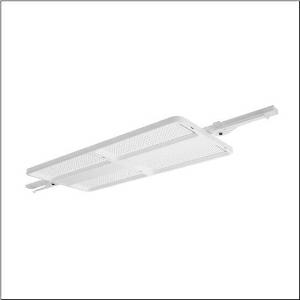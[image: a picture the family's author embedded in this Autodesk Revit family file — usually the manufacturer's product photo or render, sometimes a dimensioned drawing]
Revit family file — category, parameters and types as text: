
# Revit family: highbay_11_fur_modario_r__tragschiene_maxi_51hn11db3tma_954c
name_source: partatom
category: Lighting Fixtures
units: mm (PartAtom-declared; Revit-internal decimal feet)

## family parameters
Cut with Voids When Loaded = No
Host = Face
Light Source = No
Part Type = Normal
Room Calculation Point = No
Round Connector Dimension = Use Diameter
Shared = No

## types (1)
- --- (1 x LED, 53070 lm, 295.1 W, 3000K)
    Apparent Load = 295 VA
    CIE Flux Codes = 85 97 100 100 100
    Color Rendering = 80
    Color Temperature = 3000K
    Default Elevation = 1800 mm
    Description = high bay luminaire Highbay 11 for Modario® trunking rail maxi; direct symmetric narrow distribution, light control with lens of PMMA; UGR ≤ 22 (X = 4H | Y = 8H | S = 0.25H | reflection values 70/50/20); luminous flux: 53.070lm; light colour: 830, colour temperature: 3000K, MacAdam ≤ 2 SDCM (initial), colour rendering: CRI > 80; luminous efficacy: 179,8lm/W; rated service life: 100.000h (L95/B50) at AT= 25°C; control: DALI 2; luminaire connection: plug, 5-pole, with phase selectionmains connection: 230..240V, AC 50/60Hz; connected load: 295,1W; protection rating (complete): IP64; insulation class (complete): insulation class I (protective earthing); protection symbol: D; impact resistance: IK07; certification: CE, ENEC, VDE, UKCA; internal wiring halogen-free; luminaire corresponds to IFS (International Featured Standards) requirements for safety and quality in the food industry; LABS conformity tested according to VDMA 24364:2018-05; housing frame of high-performance plastic PA6, matt traffic white (RAL 9016); cover of PMMA; fixing on rail side of steel, galvanised, white; blank cover of PC, traffic white (RAL 9016); dimension (LxWxH): 1.496 x 442 x 72mm; permissible operating ambient temperature: -40..+50°C (reducing of maximum allowable ambient temperature of 5°C with ceiling mounting); packaging unit: 1 piece
    Height = 72 mm  [stored 0.23622 ft]
    Lamp = 1 x LED
    Lamp Light Flux = 53070 lm
    Lamp Power = 295.1 W
    Lamp count = 1
    Length = 946 mm
    Luminous efficacy = 180 lm/W
    Manufacturer = Siteco
    ModVariant = No
    Model = 51HN11DB3TMA
    Mounting Place = Ceiling
    Mounting Type = Pendant
    Number of Poles = 1
    OnlyDefault = Yes
    Power Factor = 1
    Product Name = Highbay 11 für Modario® Tragschiene maxi
    Product group = high bay luminaire
    ProductGroupID = 901
    Protection Class = Protection class I
    Protection Degree = IP 64
    RLX_Detail_Level = 1
    RLX_Emergency_Light_Flux = 0 lm
    RLX_Emergency_Type = 0
    RLX_Emergency_Type_DB = No
    RlxData = <blob elided: 21465 chars, md5=af70d04b>
    Socket = socket
    Standby Power = 0 W
    System Light Flux = 53071 lm
    System Power = 295 W
    Type Comments = factory setting: luminous flux: 100 % | dim-lin: 254 | 664 mA
    Type Image = l_1363248.jpg
    URL = http://relux.com
    VarID = @adj_004477
    Voltage = 0 V
    Weight = 0.00 kg
    Width = 442 mm

note: [stored X ft] marks values corroborated as IEEE doubles in the binary element streams (Revit-internal decimal feet)

## geometry (parser evidence)
native form markers: Blend x4, Sweep x10
no freeform markers — native parametric forms only
